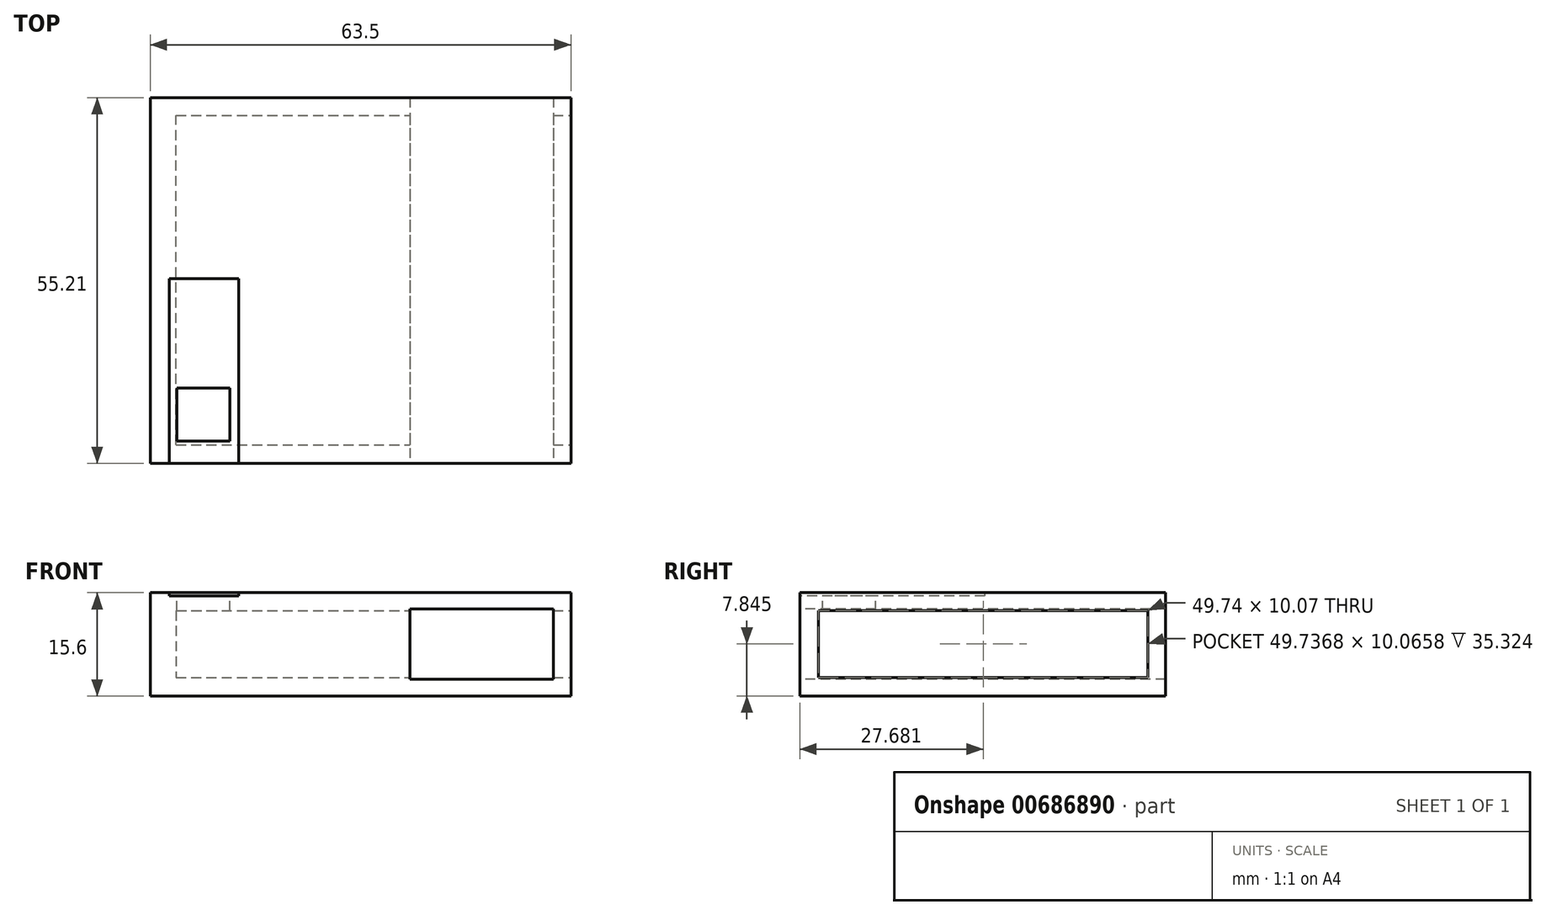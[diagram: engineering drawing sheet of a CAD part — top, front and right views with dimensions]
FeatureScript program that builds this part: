
annotation { "Feature Type Name" : "Feature", "Feature Type Description" : "" }
export const myFeature = defineFeature(function(context is Context, id is Id, definition is map)
    precondition{}
    {
        {
            var Q0;
            Q0=qCreatedBy(makeId("Top.planeOp"),FACE);
            var sketch = newSketch(context, id + "F0", { "sketchPlane" : qUnion([Q0])});
            skLineSegment(sketch, "E0.bottom", {"start": v(0, 0) * mm, "end": v(63.5, 0) * mm});
            skLineSegment(sketch, "E0.top", {"start": v(0, 55.21) * mm, "end": v(63.5, 55.21) * mm});
            skLineSegment(sketch, "E0.left", {"start": v(0, 0) * mm, "end": v(0, 55.21) * mm});
            skLineSegment(sketch, "E0.right", {"start": v(63.5, 0) * mm, "end": v(63.5, 55.21) * mm});
            skSolve(sketch);
        }
        {
            var Q0;
            Q0=makeQuery(id+"F0.imprint","IMPRINT",FACE,{"disambiguationData":[TD([[makeQuery(id+"F0.imprint","IMPRINT",EDGE,{"derivedFrom":sQuery(id+"F0.wireOp",EDGE,"E0.bottom")}),1.0]])]});
            extrude(context, id + "F1", {"entities" : qUnion([Q0]), "depth" : 15.6 * mm, "offsetDistance" : 25 * mm});
        }
        {
            var Q0;
            Q0=makeQuery(id+"F1.opExtrude","SWEPT_FACE",FACE,{"disambiguationData":[OSD([sQuery(id+"F0.wireOp",EDGE,"E0.bottom")])]});
            var sketch = newSketch(context, id + "F2", { "sketchPlane" : qUnion([Q0])});
            skLineSegment(sketch, "E1.bottom", {"start": v(39.23, 13.17) * mm, "end": v(60.84, 13.17) * mm});
            skLineSegment(sketch, "E1.top", {"start": v(39.23, 2.52) * mm, "end": v(60.84, 2.52) * mm});
            skLineSegment(sketch, "E1.left", {"start": v(39.23, 13.17) * mm, "end": v(39.23, 2.52) * mm});
            skLineSegment(sketch, "E1.right", {"start": v(60.84, 13.17) * mm, "end": v(60.84, 2.52) * mm});
            skSolve(sketch);
        }
        {
            var Q0;
            Q0=makeQuery(id+"F2.imprint","IMPRINT",FACE,{"disambiguationData":[TD([[makeQuery(id+"F2.imprint","IMPRINT",EDGE,{"derivedFrom":sQuery(id+"F2.wireOp",EDGE,"E1.bottom")}),-1.0]])]});
            extrude(context, id + "F3", {"entities" : qUnion([Q0]), "operationType" : NewBodyOperationType.REMOVE, "oppositeDirection" : true, "depth" : 60.6 * mm, "offsetDistance" : 25 * mm});
        }
        {
            var Q0;
            Q0=makeQuery(id+"F1.opExtrude","SWEPT_FACE",FACE,{"disambiguationData":[OSD([sQuery(id+"F0.wireOp",EDGE,"E0.right")])]});
            var sketch = newSketch(context, id + "F4", { "sketchPlane" : qUnion([Q0])});
            skLineSegment(sketch, "E2.bottom", {"start": v(2.81, 12.88) * mm, "end": v(52.55, 12.88) * mm});
            skLineSegment(sketch, "E2.top", {"start": v(2.81, 2.81) * mm, "end": v(52.55, 2.81) * mm});
            skLineSegment(sketch, "E2.left", {"start": v(2.81, 12.88) * mm, "end": v(2.81, 2.81) * mm});
            skLineSegment(sketch, "E2.right", {"start": v(52.55, 12.88) * mm, "end": v(52.55, 2.81) * mm});
            skSolve(sketch);
        }
        {
            var Q0;
            Q0 = qSketchRegion(id + "F4", true);
            extrude(context, id + "F5", {"entities" : qUnion([Q0]), "operationType" : NewBodyOperationType.REMOVE, "oppositeDirection" : true, "depth" : 59.6 * mm, "offsetDistance" : 25 * mm});
        }
        {
            var Q0;
            Q0=makeQuery(id+"F1.opExtrude","CAP_FACE",FACE,{"disambiguationData":[OSD([sQuery(id+"F0.wireOp",EDGE,"E0.bottom"),sQuery(id+"F0.wireOp",EDGE,"E0.top"),sQuery(id+"F0.wireOp",EDGE,"E0.left"),sQuery(id+"F0.wireOp",EDGE,"E0.right")])],"isStart":false});
            var sketch = newSketch(context, id + "F6", { "sketchPlane" : qUnion([Q0])});
            skLineSegment(sketch, "E3.bottom", {"start": v(12, 11.41) * mm, "end": v(4, 11.41) * mm});
            skLineSegment(sketch, "E3.top", {"start": v(12, 3.41) * mm, "end": v(4, 3.41) * mm});
            skLineSegment(sketch, "E3.left", {"start": v(12, 11.41) * mm, "end": v(12, 3.41) * mm});
            skLineSegment(sketch, "E3.right", {"start": v(4, 11.41) * mm, "end": v(4, 3.41) * mm});
            skSolve(sketch);
        }
        {
            var Q0;
            Q0=makeQuery(id+"F6.imprint","IMPRINT",FACE,{"disambiguationData":[TD([[makeQuery(id+"F6.imprint","IMPRINT",EDGE,{"derivedFrom":sQuery(id+"F6.wireOp",EDGE,"E3.bottom")}),1.0]])]});
            extrude(context, id + "F7", {"entities" : qUnion([Q0]), "operationType" : NewBodyOperationType.REMOVE, "oppositeDirection" : true, "depth" : 6.1 * mm, "offsetDistance" : 25 * mm});
        }
        {
            var Q0;
            Q0=makeQuery(id+"F1.opExtrude","SWEPT_FACE",FACE,{"disambiguationData":[OSD([sQuery(id+"F0.wireOp",EDGE,"E0.bottom")])]});
            var sketch = newSketch(context, id + "F8", { "sketchPlane" : qUnion([Q0])});
            skLineSegment(sketch, "E4.bottom", {"start": v(2.87, 15.6) * mm, "end": v(13.37, 15.6) * mm});
            skLineSegment(sketch, "E4.top", {"start": v(2.87, 15.12) * mm, "end": v(13.37, 15.12) * mm});
            skLineSegment(sketch, "E4.left", {"start": v(2.87, 15.6) * mm, "end": v(2.87, 15.12) * mm});
            skLineSegment(sketch, "E4.right", {"start": v(13.37, 15.6) * mm, "end": v(13.37, 15.12) * mm});
            skSolve(sketch);
        }
        {
            var Q0;
            Q0 = qSketchRegion(id + "F8", true);
            extrude(context, id + "F9", {"entities" : qUnion([Q0]), "operationType" : NewBodyOperationType.REMOVE, "oppositeDirection" : true, "depth" : 27.9 * mm, "offsetDistance" : 25 * mm});
        }
    });
